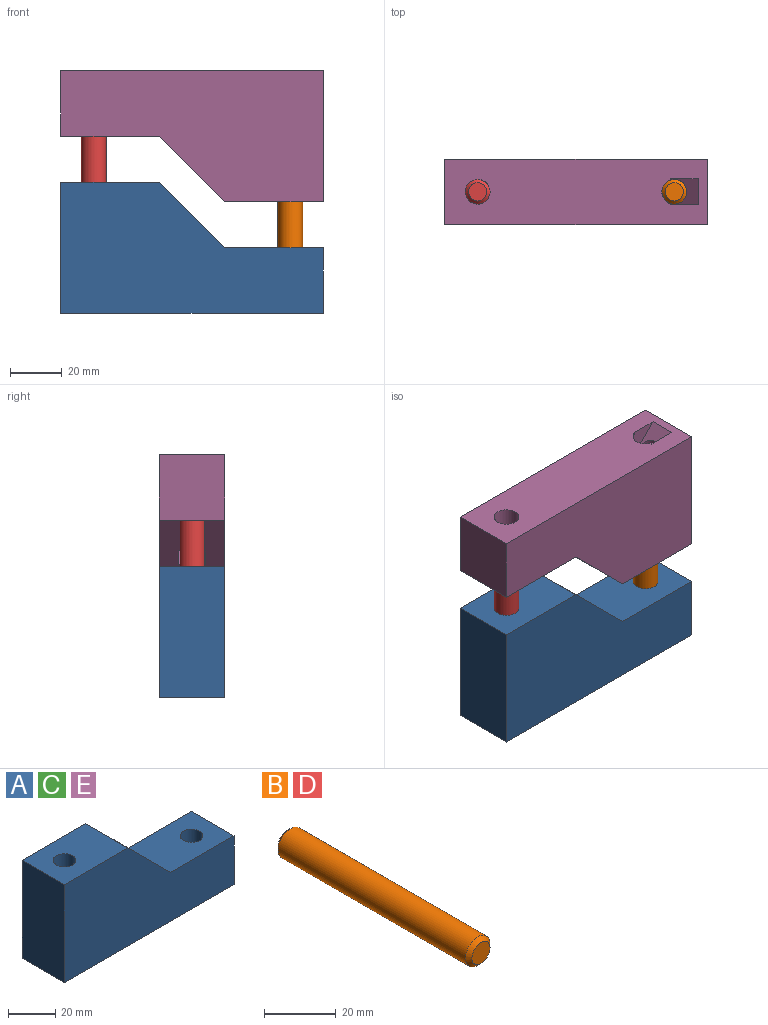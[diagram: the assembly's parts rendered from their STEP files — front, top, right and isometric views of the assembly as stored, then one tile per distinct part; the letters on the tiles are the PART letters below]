
ASSEMBLY  parts=5 mates=4
PART A: 15 faces, bbox 101.6x25.4x50.8 mm
  f0: plane 25.4x25.4mm, normal (0.71,0,0.71), area 835mm2, adj f3,f4,f7,f8,f11,f12,f13,f14
  f1: plane 101.6x25.4mm, normal (0,0,-1), area 2376mm2, adj f2,f5,f6,f7,f8,f10,f11,f12
  f2: cylinder r=4.83mm len=9.15mm, axis (0,0,1), area 25.6mm2, adj f1,f13
  f3: plane 38.1x25.4mm, normal (0,0,1), area 894.6mm2, adj f0,f6,f7,f8,f10
  f4: plane 38.1x25.4mm, normal (0,0,1), area 894.6mm2, adj f0,f5,f7,f8,f9
  f5: plane 50.8x25.4mm, normal (-1,0,0), area 1290.3mm2, adj f1,f4,f7,f8
  f6: plane 25.4x25.4mm, normal (1,0,0), area 645.2mm2, adj f1,f3,f7,f8
  f7: plane 101.6x50.8mm, normal (0,-1,0), area 3871mm2, adj f0,f1,f3,f4,f5,f6
  f8: plane 101.6x50.8mm, normal (0,1,0), area 3871mm2, adj f0,f1,f3,f4,f5,f6
  f9: cylinder r=4.83mm len=46.46mm, axis (0,0,1), area 1260.3mm2, adj f4,f14
  f10: cylinder r=4.83mm len=25.4mm, axis (0,0,1), area 770.2mm2, adj f1,f3
  f11: plane 48.11x42.72mm, normal (0,-1,0), area 431.3mm2, adj f0,f1,f13,f14
  f12: plane 48.11x42.72mm, normal (0,1,0), area 431.3mm2, adj f0,f1,f13,f14
  f13: plane 37.33x37.33mm, normal (-0.71,0,0.71), area 505.3mm2, adj f0,f1,f2,f11,f12
  f14: plane 42.72x42.72mm, normal (0.71,0,-0.71), area 510.3mm2, adj f0,f1,f9,f11,f12
PART B: 5 faces, bbox 9.7x76.2x9.7 mm
  f0: cylinder r=4.83mm len=73.66mm, axis (0,-1,0), area 2233.6mm2, adj f3,f4
  f1: plane 7.11x7.11mm, normal (0,1,0), area 39.7mm2, adj f3
  f2: plane 7.11x7.11mm, normal (0,-1,0), area 39.7mm2, adj f4
  f3: cone r=4.83mm half-angle=45deg, axis (0,-1,0), area 47.3mm2, adj f0,f1
  f4: cone r=3.56mm half-angle=45deg, axis (0,1,0), area 47.3mm2, adj f0,f2
PART C: same geometry as A
PART D: same geometry as B
PART E: same geometry as A
PLACE A t=(17.07,-42.39,-21.21)mm
PLACE B rot(axis=(-1,0,0),90deg) t=(105.97,-55.09,4.51)mm
PLACE C t=(17.07,-42.39,-21.21)mm
PLACE D rot(axis=(-1,0,0),90deg) t=(29.77,-55.09,4.26)mm
PLACE E rot(axis=(0,-1,0),180deg) t=(118.67,-42.39,-28.76)mm
MATE cylindrical D.f0 <-> C.f2  axis (0,0,1) through (29.77,-55.09,-33.84)mm
MATE cylindrical B.f0 <-> E.f2  axis (0,0,1) through (105.97,-55.09,3.24)mm
MATE cylindrical B.f0 <-> C.f10  axis (0,0,1) through (105.97,-55.09,-33.59)mm
MATE cylindrical D.f0 <-> E.f10  axis (0,0,1) through (29.77,-55.09,-33.84)mm
